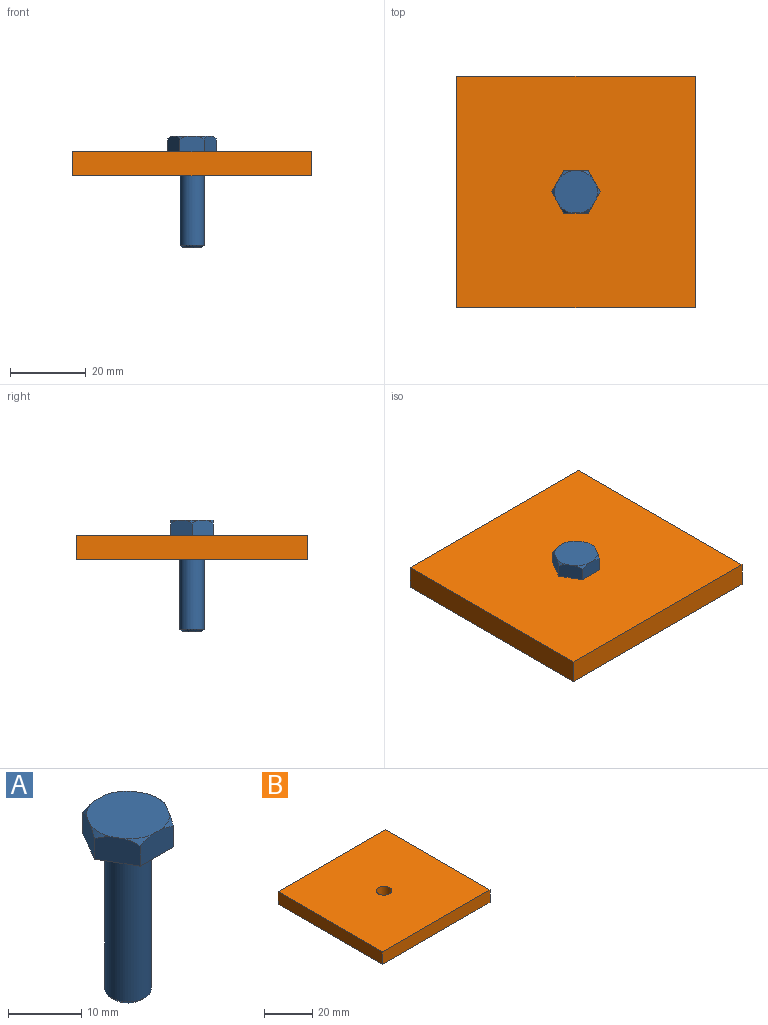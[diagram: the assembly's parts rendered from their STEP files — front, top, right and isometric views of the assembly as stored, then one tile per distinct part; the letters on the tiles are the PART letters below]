
ASSEMBLY  parts=2 mates=1
PART A: 18 faces, bbox 12.9x12.6x29.5 mm
  f0: plane 5.08x5.08mm, normal (0,0,-1), area 20.3mm2, adj f17
  f1: cylinder r=3.17mm len=24.45mm, axis (0,0,-1), area 487.7mm2, adj f16,f17
  f2: plane 12.85x11.13mm, normal (0,0,-1), area 68.9mm2, adj f3,f4,f5,f6,f7,f8,f16
  f3: plane 5.57x4.14mm, normal (0.87,0.5,0), area 25.2mm2, adj f2,f4,f6,f9,f13,f15
  f4: plane 6.43x4.14mm, normal (0,1,0), area 25.2mm2, adj f2,f3,f5,f9,f14,f15
  f5: plane 5.57x4.14mm, normal (-0.87,0.5,0), area 25.2mm2, adj f2,f4,f7,f9,f12,f14
  f6: plane 5.57x4.14mm, normal (0.87,-0.5,0), area 25.2mm2, adj f2,f3,f8,f9,f11,f13
  f7: plane 5.57x4.14mm, normal (-0.87,-0.5,0), area 25.2mm2, adj f2,f5,f8,f9,f10,f12
  f8: plane 6.43x4.14mm, normal (0,-1,0), area 25.2mm2, adj f2,f6,f7,f9,f10,f11
  f9: plane 11.32x11.13mm, normal (0,0,1), area 99.9mm2, adj f3,f4,f5,f6,f7,f8,f10,f11
  f10: cone r=5.66mm half-angle=45deg, axis (0,0,-1), area 1.7mm2, adj f7,f8,f9
  f11: cone r=5.66mm half-angle=45deg, axis (0,0,-1), area 1.7mm2, adj f6,f8,f9
  f12: cone r=5.66mm half-angle=45deg, axis (0,0,-1), area 1.7mm2, adj f5,f7,f9
  f13: cone r=5.66mm half-angle=45deg, axis (0,0,-1), area 1.7mm2, adj f3,f6,f9
  f14: cone r=5.66mm half-angle=45deg, axis (0,0,-1), area 1.7mm2, adj f4,f5,f9
  f15: cone r=5.66mm half-angle=45deg, axis (0,0,-1), area 1.7mm2, adj f3,f4,f9
  f16: torus R=3.49mm, axis (0,0,1), area 10.3mm2, adj f1,f2
  f17: cone r=2.54mm half-angle=45deg, axis (0,0,1), area 16.1mm2, adj f0,f1
PART B: 7 faces, bbox 63x61.1x6.4 mm
  f0: plane 61.14x6.35mm, normal (1,0,0), area 388.2mm2, adj f1,f4,f5,f6
  f1: plane 62.96x6.35mm, normal (0,1,0), area 399.8mm2, adj f0,f2,f5,f6
  f2: plane 61.14x6.35mm, normal (-1,0,0), area 388.2mm2, adj f1,f4,f5,f6
  f3: cylinder r=3.17mm len=6.35mm, axis (0,0,1), area 126.7mm2, adj f5,f6
  f4: plane 62.96x6.35mm, normal (0,-1,0), area 399.8mm2, adj f0,f2,f5,f6
  f5: plane 62.96x61.14mm, normal (0,0,-1), area 3817.4mm2, adj f0,f1,f2,f3,f4
  f6: plane 62.96x61.14mm, normal (0,0,1), area 3817.4mm2, adj f0,f1,f2,f3,f4
PLACE A t=(-45.78,-14.69,6.01)mm
PLACE B t=(-45.78,-14.69,31.41)mm fixed
MATE revolute B.f3 <-> A.f1  axis (0,0,1) through (-45.78,-14.69,31.41)mm
